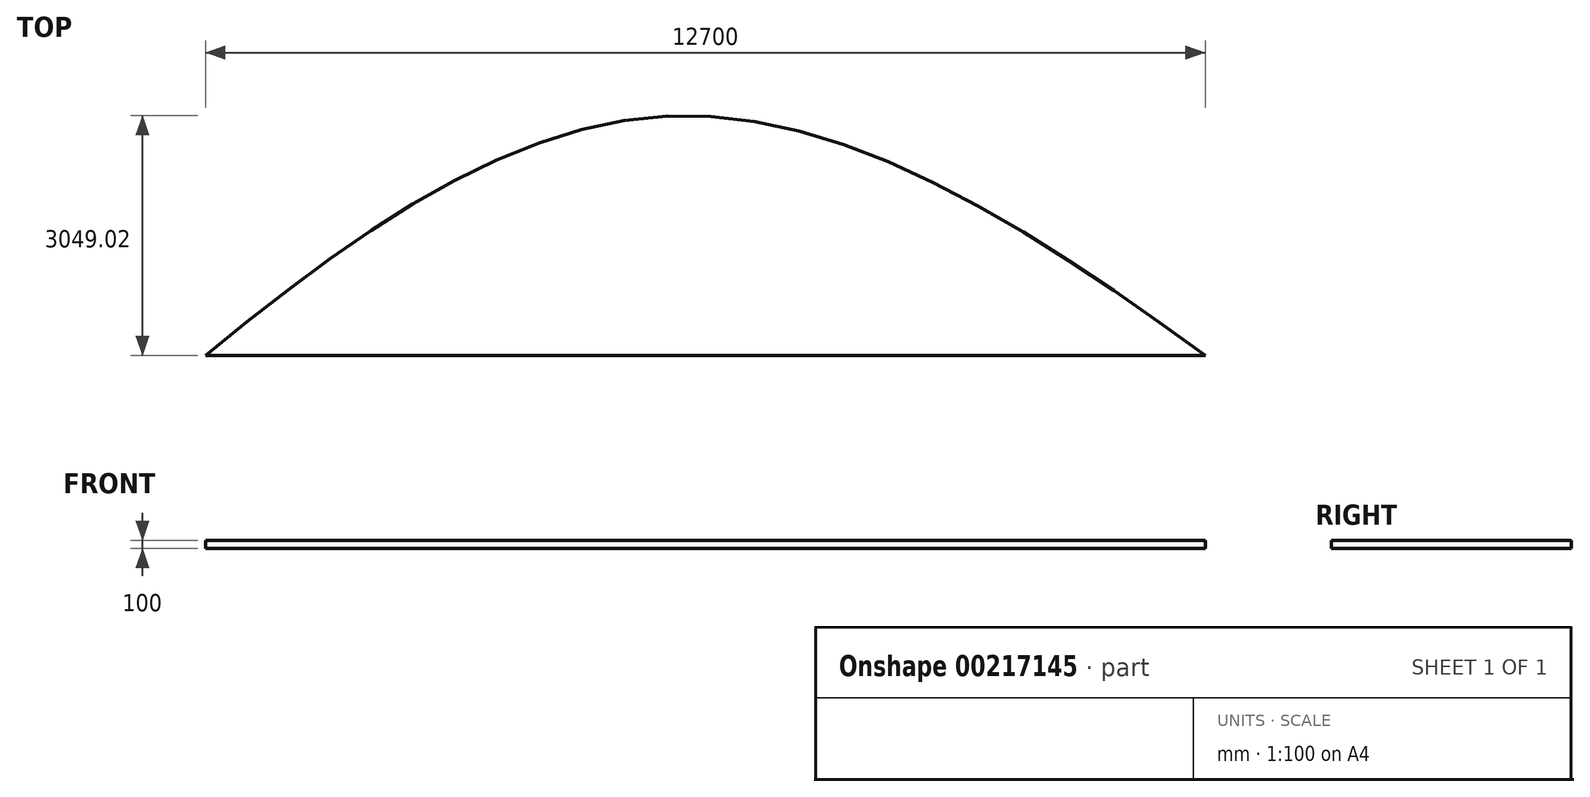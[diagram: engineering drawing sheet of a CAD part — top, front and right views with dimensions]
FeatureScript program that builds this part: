
annotation { "Feature Type Name" : "Feature", "Feature Type Description" : "" }
export const myFeature = defineFeature(function(context is Context, id is Id, definition is map)
    precondition{}
    {
        {
            var Q0;
            Q0=qCreatedBy(makeId("Top.planeOp"),FACE);
            var sketch = newSketch(context, id + "F0", { "sketchPlane" : qUnion([Q0])});
            skLineSegment(sketch, "E0", {"start": v(-6002.58, 0) * mm, "end": v(6697.42, 0) * mm});
            skFitSpline(sketch, "E1", {"points": [v(6697.42, 0) * mm, v(0, 3048) * mm, v(-6002.58, 0) * mm], "startDerivative": vector(-13326.93, 9789.47) * mm, "endDerivative": vector(-12063.99, -9931.32) * mm});
            skSolve(sketch);
        }
        {
            var Q0;
            Q0=makeQuery(id+"F0.imprint","IMPRINT",FACE,{"disambiguationData":[TD([[makeQuery(id+"F0.imprint","IMPRINT",EDGE,{"derivedFrom":sQuery(id+"F0.wireOp",EDGE,"E0")}),1.0]])]});
            extrude(context, id + "F1", {"entities" : qUnion([Q0]), "depth" : 100 * mm});
        }
    });
